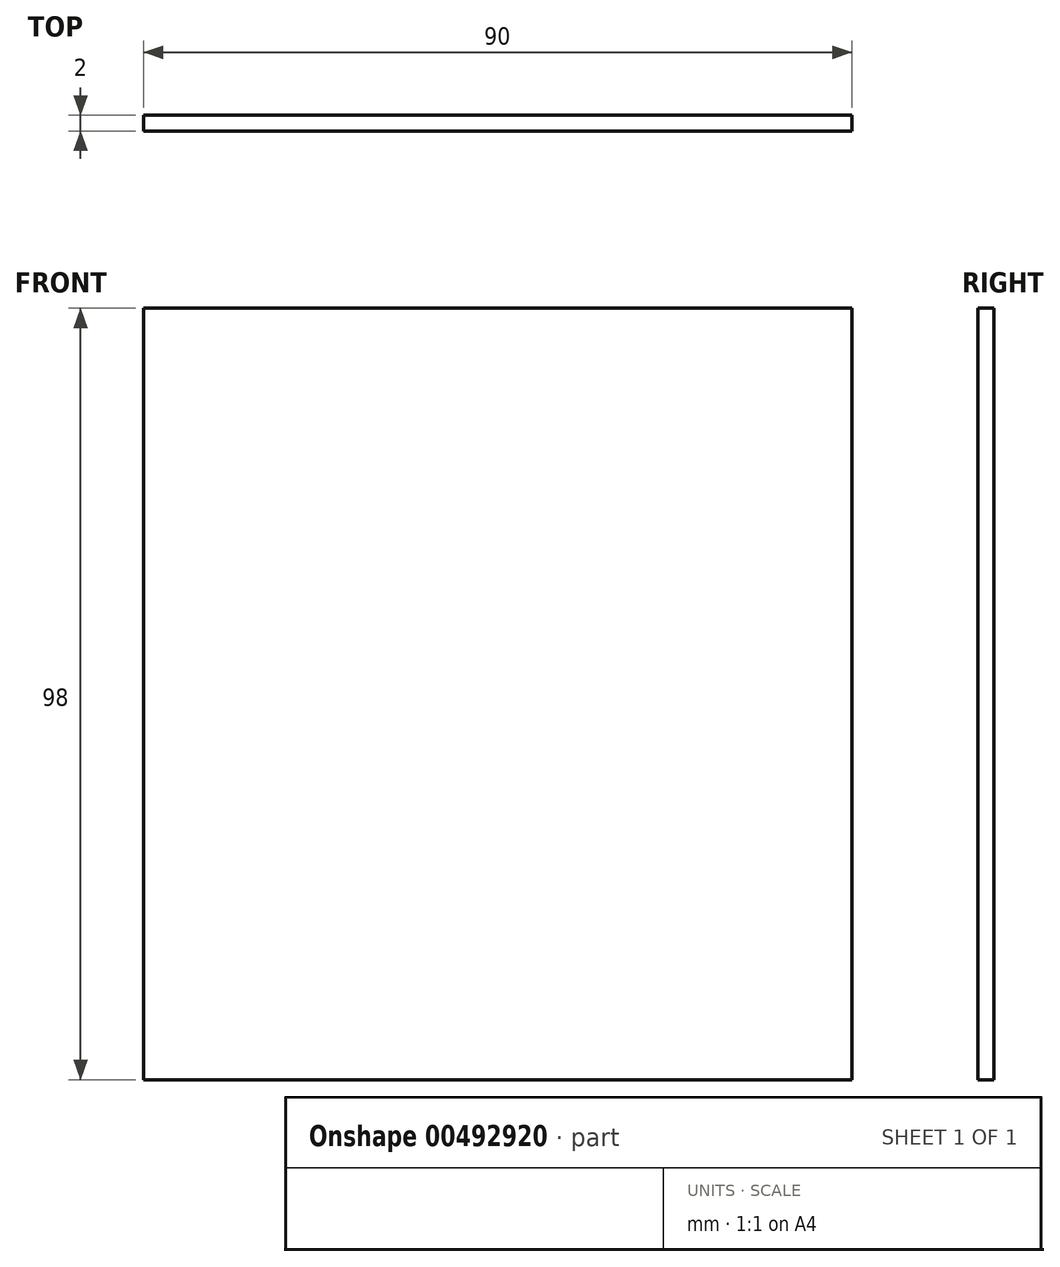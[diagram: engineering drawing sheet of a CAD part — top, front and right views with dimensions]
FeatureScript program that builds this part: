
annotation { "Feature Type Name" : "Feature", "Feature Type Description" : "" }
export const myFeature = defineFeature(function(context is Context, id is Id, definition is map)
    precondition{}
    {
        {
            var Q0;
            Q0=qCreatedBy(makeId("Top.planeOp"),FACE);
            var sketch = newSketch(context, id + "F0", { "sketchPlane" : qUnion([Q0])});
            skLineSegment(sketch, "E0.bottom", {"start": v(45, -1) * mm, "end": v(-45, -1) * mm});
            skLineSegment(sketch, "E0.top", {"start": v(45, 1) * mm, "end": v(-45, 1) * mm});
            skLineSegment(sketch, "E0.left", {"start": v(45, -1) * mm, "end": v(45, 1) * mm});
            skLineSegment(sketch, "E0.right", {"start": v(-45, -1) * mm, "end": v(-45, 1) * mm});
            skPoint(sketch, "E0.middle", {"position": v(0, 0) * mm});
            skSolve(sketch);
        }
        {
            var Q0;
            Q0=makeQuery(id+"F0.imprint","IMPRINT",FACE,{"disambiguationData":[TD([[makeQuery(id+"F0.imprint","IMPRINT",EDGE,{"derivedFrom":sQuery(id+"F0.wireOp",EDGE,"E0.bottom")}),-1.0]])]});
            extrude(context, id + "F1", {"entities" : qUnion([Q0]), "depth" : 98 * mm, "offsetDistance" : 25 * mm});
        }
    });
